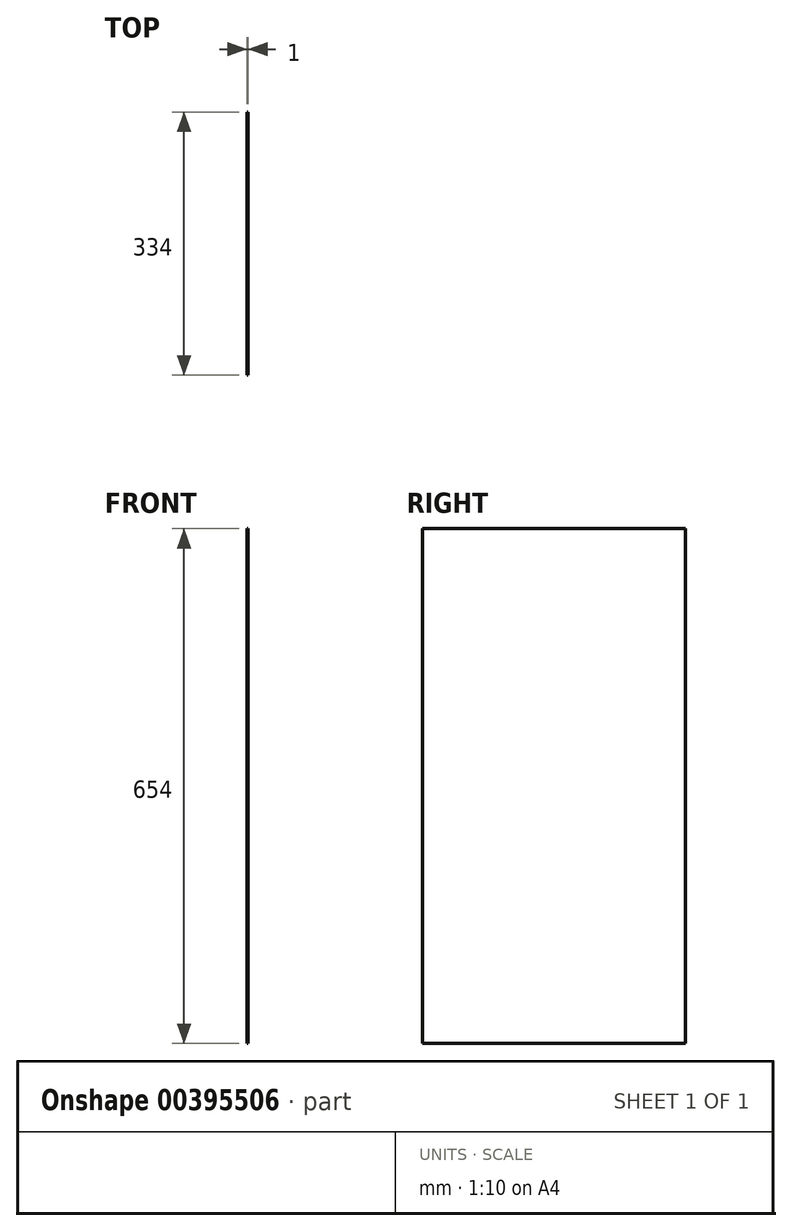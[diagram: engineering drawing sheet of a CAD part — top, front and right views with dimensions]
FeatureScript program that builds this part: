
annotation { "Feature Type Name" : "Feature", "Feature Type Description" : "" }
export const myFeature = defineFeature(function(context is Context, id is Id, definition is map)
    precondition{}
    {
        {
            var Q0;
            Q0=qCreatedBy(makeId("Right.planeOp"),FACE);
            var sketch = newSketch(context, id + "F0", { "sketchPlane" : qUnion([Q0])});
            skLineSegment(sketch, "E0.bottom", {"start": v(167, -327) * mm, "end": v(-167, -327) * mm});
            skLineSegment(sketch, "E0.top", {"start": v(167, 327) * mm, "end": v(-167, 327) * mm});
            skLineSegment(sketch, "E0.left", {"start": v(167, -327) * mm, "end": v(167, 327) * mm});
            skLineSegment(sketch, "E0.right", {"start": v(-167, -327) * mm, "end": v(-167, 327) * mm});
            skPoint(sketch, "E0.middle", {"position": v(0, 0) * mm});
            skSolve(sketch);
        }
        {
            var Q0;
            Q0=makeQuery(id+"F0.imprint","IMPRINT",FACE,{"disambiguationData":[TD([[makeQuery(id+"F0.imprint","IMPRINT",EDGE,{"derivedFrom":sQuery(id+"F0.wireOp",EDGE,"E0.bottom")}),-1.0]])]});
            extrude(context, id + "F1", {"entities" : qUnion([Q0]), "depth" : 1 * mm});
        }
    });
